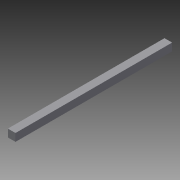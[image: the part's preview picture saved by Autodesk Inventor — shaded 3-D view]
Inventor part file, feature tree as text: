
AUTODESK INVENTOR PART (.ipt)
format: ipt  version: 2015 (Build 190159000, 159)  size: 68,096 bytes
history: native  units: in
note: dims shown in document units (in); Inventor stores cm internally (conversion verified against a paired STEP export)
features: extrude x1, sketch x1
ambient origin geometry x8: Origin, YZ Plane, XZ Plane, XY Plane, X Axis, Y Axis, Z Axis, Center Point
bodies: Solid1 (feature_tree)
feature tree (2):
  extrude  "Extrusion1"  Depth=0.75in
  sketch  "Sketch1"  dims[d0=0.75in d1=0.75in d2=15.375in d3=0.0in]
